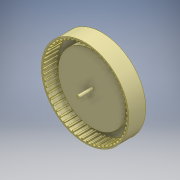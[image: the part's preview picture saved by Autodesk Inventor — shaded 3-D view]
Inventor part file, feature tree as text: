
AUTODESK INVENTOR PART (.ipt)
format: ipt  version: 2016 (Build 200138000, 138)  size: 337,920 bytes
history: native  units: mm
features: extrude x6, sketch x6, other x1, pattern_circular x1
ambient origin geometry x8: Origin, YZ Plane, XZ Plane, XY Plane, X Axis, Y Axis, Z Axis, Center Point
bodies: Body1 (feature_tree)
feature tree (14):
  other  "Sólido1"
  extrude  "Extrusión1"  Depth=2.0mm TaperAngle=0.0deg
  extrude  "Extrusión2"  Depth=60.0mm
  extrude  "Extrusión3"  Depth=10.0mm TaperAngle=0.0deg
  pattern_circular  "Patrón circular1"  Count=55 Angle=360.0deg
  extrude  "Extrusión5"  Depth=3.0mm
  extrude  "Extrusión6"  Depth=2.0mm
  extrude  "Extrusión7"  Depth=15.0mm TaperAngle=0.0deg
  sketch  "Boceto1"  dims[d0=62.0mm d1=2.0mm d2=0.0mm]
  sketch  "Boceto2"  dims[d3=62.0mm d4=60.0mm]
  sketch  "Boceto4"  dims[d5=2.0mm d6=10.0mm d7=0.0mm]
  sketch  "Boceto6"  dims[d8=1.0mm]
  sketch  "Boceto7"  dims[d9=1.0mm]
  sketch  "Boceto8"  dims[d10=10.0mm d11=0.0mm d12=550.0mm d13=360.0deg d18=19.198622mm d20=12.217305mm d26=2.0mm d27=15.0mm d28=0.0mm d29=48.0mm d30=5.0mm d31=0.0mm d32=46.0mm d33=3.0mm d34=0.0mm d35=46.0mm]
